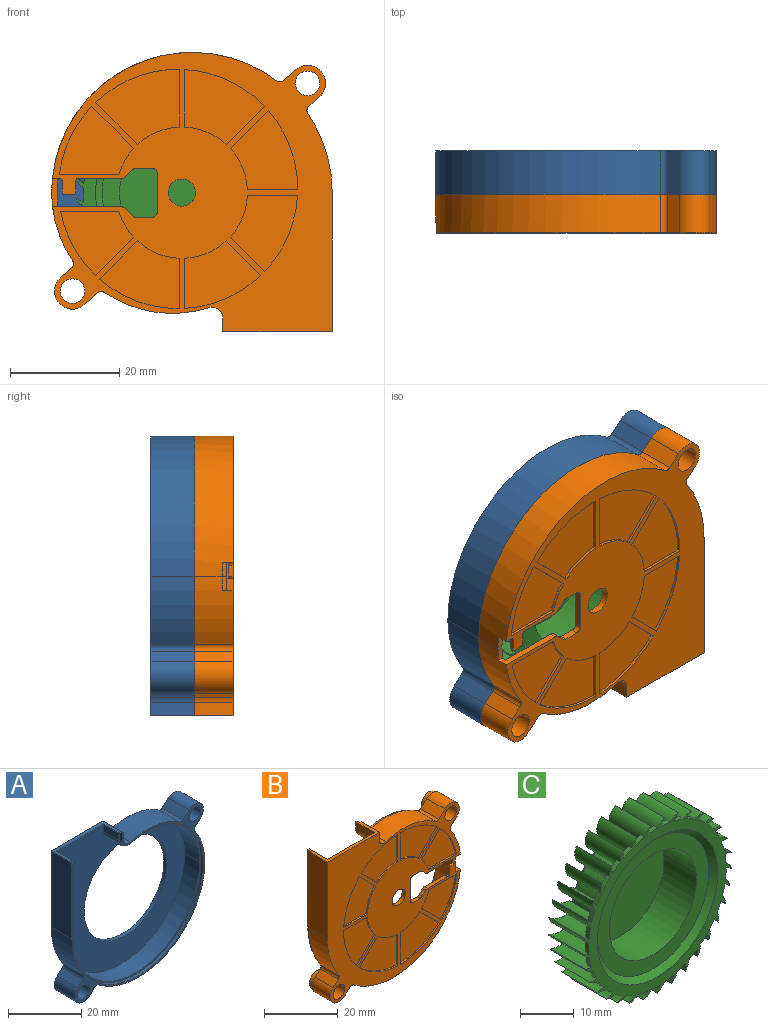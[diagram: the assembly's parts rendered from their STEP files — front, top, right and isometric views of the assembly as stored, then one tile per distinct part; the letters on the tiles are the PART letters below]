
ASSEMBLY  parts=3 mates=2
PART A: 35 faces, bbox 51.3x8x51.1 mm
  f0: cylinder r=25.15mm len=50.3mm, axis (0,-1,0), area 79mm2, adj f28,f32,f33,f34
  f1: cylinder r=2.5mm len=3.25mm, axis (0,-1,0), area 4.7mm2, adj f28,f31,f32,f34
  f2: cylinder r=2.25mm len=8mm, axis (0,1,0), area 113.1mm2, adj f28,f29
  f3: cylinder r=2.25mm len=8mm, axis (0,1,0), area 113.1mm2, adj f28,f29
  f4: cylinder r=22.07mm len=19.05mm, axis (0,1,0), area 159.4mm2, adj f20,f21,f28,f29
  f5: cylinder r=3.3mm len=8mm, axis (0,1,0), area 82.9mm2, adj f18,f19,f28,f29
  f6: cylinder r=1mm len=8mm, axis (0,1,0), area 11mm2, adj f14,f15,f28,f29
  f7: cylinder r=16mm len=32mm, axis (0,1,0), area 120.6mm2, adj f29,f30
  f8: cylinder r=24.65mm len=49.3mm, axis (0,-1,0), area 449.3mm2, adj f11,f12,f30,f34
  f9: cylinder r=3mm len=5.8mm, axis (0,-1,0), area 32.6mm2, adj f10,f11,f30,f34
  f10: plane 5.8x2.44mm, normal (-1,0,0), area 14.2mm2, adj f9,f23,f30,f34
  f11: cylinder r=21.07mm len=27.4mm, axis (0,-1,0), area 229.2mm2, adj f8,f9,f30,f34
  f12: plane 25.4x5.8mm, normal (1,0,0), area 147.3mm2, adj f8,f23,f30,f34
  f13: cylinder r=3.3mm len=8mm, axis (0,1,0), area 82.9mm2, adj f14,f27,f28,f29
  f14: plane 8x2.22mm, normal (0.66,0,-0.75), area 23.7mm2, adj f6,f13,f28,f29
  f15: cylinder r=25.65mm len=41.13mm, axis (0,1,0), area 455.4mm2, adj f6,f16,f28,f29
  f16: cylinder r=22.07mm len=12.41mm, axis (0,1,0), area 105.5mm2, adj f15,f17,f28,f29
  f17: cylinder r=1mm len=8mm, axis (0,1,0), area 11.6mm2, adj f16,f18,f28,f29
  f18: plane 8x2.04mm, normal (0.66,0,-0.75), area 21.8mm2, adj f5,f17,f28,f29
  f19: plane 8x2.44mm, normal (-0.66,0,0.75), area 26mm2, adj f5,f20,f28,f29
  f20: cylinder r=1mm len=8mm, axis (0,1,0), area 10.6mm2, adj f4,f19,f28,f29
  f21: cylinder r=2mm len=8mm, axis (0,1,0), area 30mm2, adj f4,f22,f28,f29
  f22: plane 8x2.44mm, normal (1,0,0), area 19.6mm2, adj f21,f23,f28,f29
  f23: plane 20x8mm, normal (0,0,1), area 36.6mm2, adj f10,f12,f22,f24,f28,f29,f30,f31
  f24: plane 25.4x8mm, normal (-1,0,0), area 203.2mm2, adj f23,f25,f28,f29
  f25: cylinder r=25.65mm len=14.47mm, axis (0,1,0), area 122.9mm2, adj f24,f26,f28,f29
  f26: cylinder r=1mm len=8mm, axis (0,1,0), area 11.6mm2, adj f25,f27,f28,f29
  f27: plane 8x1.98mm, normal (-0.66,0,0.75), area 21.1mm2, adj f13,f26,f28,f29
  f28: plane 51.3x51.07mm, normal (0,-1,0), area 126.8mm2, adj f0,f1,f2,f3,f4,f5,f6,f13
  f29: plane 51.3x51.07mm, normal (0,1,0), area 1370.5mm2, adj f2,f3,f4,f5,f6,f7,f13,f14
  f30: plane 50.07x49.3mm, normal (0,-1,0), area 1168mm2, adj f7,f8,f9,f10,f11,f12,f23
  f31: plane 2.44x1mm, normal (-1,0,0), area 2.4mm2, adj f1,f23,f28,f34
  f32: cylinder r=21.57mm len=28.05mm, axis (0,-1,0), area 40.5mm2, adj f0,f1,f28,f34
  f33: plane 25.4x1mm, normal (1,0,0), area 25.4mm2, adj f0,f23,f28,f34
  f34: plane 50.57x50.3mm, normal (0,-1,0), area 75.6mm2, adj f0,f1,f8,f9,f10,f11,f12,f23
PART B: 104 faces, bbox 52.9x8.5x51.4 mm
  f0: torus R=1.41mm, axis (0,-1,0), area 1.6mm2, adj f31,f35,f102,f103
  f1: cylinder r=21.88mm len=15.3mm, axis (0,-1,0), area 8.4mm2, adj f14,f53,f54,f55
  f2: cylinder r=2.82mm len=5.65mm, axis (0,-1,0), area 26.6mm2, adj f15,f41
  f3: cylinder r=2.82mm len=5.65mm, axis (0,-1,0), area 26.6mm2, adj f15,f40
  f4: cylinder r=21.57mm len=28.05mm, axis (0,1,0), area 40.5mm2, adj f15,f16,f37,f38
  f5: cylinder r=21.07mm len=27.4mm, axis (0,1,0), area 266.7mm2, adj f16,f31,f33,f34,f86,f87
  f6: cylinder r=2.5mm len=5mm, axis (0,-1,0), area 18.8mm2, adj f14,f31
  f7: cylinder r=2.25mm len=8.5mm, axis (0,-1,0), area 120.2mm2, adj f14,f40
  f8: cylinder r=2.25mm len=8.5mm, axis (0,-1,0), area 120.2mm2, adj f14,f41
  f9: cylinder r=25.65mm len=41.13mm, axis (0,-1,0), area 393.3mm2, adj f13,f14,f15,f28,f29,f87
  f10: cylinder r=1mm len=7mm, axis (0,-1,0), area 9.3mm2, adj f14,f15,f23,f24
  f11: cylinder r=2mm len=7mm, axis (0,-1,0), area 26.3mm2, adj f14,f15,f22,f23
  f12: cylinder r=3.3mm len=7mm, axis (0,-1,0), area 72.6mm2, adj f14,f15,f17,f30
  f13: plane 12.66x2mm, normal (0,0,1), area 13.2mm2, adj f9,f14,f31,f34,f87,f93,f95,f98
  f14: plane 51.17x51.07mm, normal (0,-1,0), area 1131.7mm2, adj f1,f6,f7,f8,f9,f10,f11,f12
  f15: plane 51.3x51.07mm, normal (0,1,0), area 108.5mm2, adj f2,f3,f4,f9,f10,f11,f12,f17
  f16: plane 50.57x50.3mm, normal (0,1,0), area 75.6mm2, adj f4,f5,f21,f32,f33,f34,f35,f36
  f17: plane 7x1.98mm, normal (-0.66,0,0.75), area 18.5mm2, adj f12,f14,f15,f18
  f18: cylinder r=1mm len=7mm, axis (0,-1,0), area 10.1mm2, adj f14,f15,f17,f19
  f19: cylinder r=25.65mm len=14.47mm, axis (0,-1,0), area 107.6mm2, adj f14,f15,f18,f20
  f20: plane 25.4x7mm, normal (-1,0,0), area 177.8mm2, adj f14,f15,f19,f21
  f21: plane 20x8mm, normal (0,0,1), area 31.2mm2, adj f14,f15,f16,f20,f22,f32,f35,f36
  f22: plane 7x2.44mm, normal (1,0,0), area 17.1mm2, adj f11,f14,f15,f21
  f23: cylinder r=22.07mm len=19.05mm, axis (0,-1,0), area 139.5mm2, adj f10,f11,f14,f15
  f24: plane 7x2.44mm, normal (-0.66,0,0.75), area 22.8mm2, adj f10,f14,f15,f25
  f25: cylinder r=3.3mm len=7mm, axis (0,-1,0), area 72.6mm2, adj f14,f15,f24,f26
  f26: plane 7x2.04mm, normal (0.66,0,-0.75), area 19.1mm2, adj f14,f15,f25,f27
  f27: cylinder r=1mm len=7mm, axis (0,-1,0), area 10.1mm2, adj f14,f15,f26,f28
  f28: cylinder r=22.07mm len=12.41mm, axis (0,-1,0), area 87.1mm2, adj f9,f14,f15,f27,f86,f87
  f29: cylinder r=1mm len=7mm, axis (0,-1,0), area 9.6mm2, adj f9,f14,f15,f30
  f30: plane 7x2.22mm, normal (0.66,0,-0.75), area 20.7mm2, adj f12,f14,f15,f29
  f31: plane 49.16x46.35mm, normal (0,1,0), area 1650.7mm2, adj f0,f5,f6,f13,f33,f34,f35,f81
  f32: plane 7.1x2.44mm, normal (-1,0,0), area 17.4mm2, adj f16,f21,f33,f102
  f33: cylinder r=3mm len=7.1mm, axis (0,1,0), area 38.5mm2, adj f5,f16,f31,f32,f103
  f34: cylinder r=24.65mm len=49.3mm, axis (0,1,0), area 524.7mm2, adj f5,f13,f16,f31,f35,f87
  f35: plane 25.4x7.1mm, normal (1,0,0), area 179.6mm2, adj f0,f16,f21,f31,f34,f102
  f36: plane 25.4x1mm, normal (-1,0,0), area 25.4mm2, adj f15,f16,f21,f37
  f37: cylinder r=25.15mm len=50.3mm, axis (0,1,0), area 79mm2, adj f4,f15,f16,f36
  f38: cylinder r=2.5mm len=3.25mm, axis (0,1,0), area 4.7mm2, adj f4,f15,f16,f39
  f39: plane 2.44x1mm, normal (1,0,0), area 2.4mm2, adj f15,f16,f21,f38
  f40: plane 5.65x5.65mm, normal (0,1,0), area 9.2mm2, adj f3,f7
  f41: plane 5.65x5.65mm, normal (0,1,0), area 9.2mm2, adj f2,f8
  f42: plane 6.99x6.99mm, normal (0.71,0,-0.71), area 4.9mm2, adj f14,f43,f45,f46
  f43: cylinder r=12mm len=7.62mm, axis (0,-1,0), area 4.2mm2, adj f14,f42,f44,f46
  f44: plane 10.54x0.5mm, normal (-1,0,0), area 5.3mm2, adj f14,f43,f45,f46
  f45: cylinder r=21.88mm len=14.61mm, axis (0,-1,0), area 8.2mm2, adj f14,f42,f44,f46
  f46: plane 14.61x13.7mm, normal (0,-1,0), area 127.2mm2, adj f42,f43,f44,f45
  f47: plane 7.67x7.67mm, normal (0.71,0,0.71), area 5.4mm2, adj f14,f48,f50,f51
  f48: cylinder r=12mm len=4.77mm, axis (0,-1,0), area 2.8mm2, adj f14,f47,f49,f51
  f49: plane 10.88x0.5mm, normal (0,0,-1), area 5.4mm2, adj f14,f48,f50,f51
  f50: cylinder r=21.88mm len=12.45mm, axis (0,-1,0), area 7mm2, adj f14,f47,f49,f51
  f51: plane 13.57x12.45mm, normal (0,-1,0), area 105.4mm2, adj f47,f48,f49,f50
  f52: cylinder r=12mm len=7.62mm, axis (0,-1,0), area 4.2mm2, adj f14,f53,f54,f55
  f53: plane 7.67x7.67mm, normal (-0.71,0,-0.71), area 5.4mm2, adj f1,f14,f52,f55
  f54: plane 10.57x0.5mm, normal (1,0,0), area 5.3mm2, adj f1,f14,f52,f55
  f55: plane 15.3x13.73mm, normal (0,-1,0), area 135.9mm2, adj f1,f52,f53,f54
  f56: cylinder r=12mm len=7.62mm, axis (0,-1,0), area 4.2mm2, adj f14,f57,f59,f60
  f57: plane 9.2x0.5mm, normal (1,0,0), area 4.6mm2, adj f14,f56,f58,f60
  f58: cylinder r=21.88mm len=14.58mm, axis (0,-1,0), area 7.9mm2, adj f14,f57,f59,f60
  f59: plane 6.96x6.96mm, normal (-0.71,0,0.71), area 4.9mm2, adj f14,f56,f58,f60
  f60: plane 14.58x12.36mm, normal (0,-1,0), area 115.4mm2, adj f56,f57,f58,f59
  f61: cylinder r=12mm len=4.77mm, axis (0,-1,0), area 2.8mm2, adj f14,f62,f64,f65
  f62: plane 6.99x6.99mm, normal (0.71,0,-0.71), area 4.9mm2, adj f14,f61,f63,f65
  f63: cylinder r=21.88mm len=11.76mm, axis (0,-1,0), area 6.8mm2, adj f14,f62,f64,f65
  f64: plane 10.66x0.5mm, normal (0,0,1), area 5.3mm2, adj f14,f61,f63,f65
  f65: plane 13.36x11.76mm, normal (0,-1,0), area 97mm2, adj f61,f62,f63,f64
  f66: cylinder r=12mm len=7.62mm, axis (0,-1,0), area 4.2mm2, adj f14,f67,f69,f70
  f67: plane 9.17x0.5mm, normal (0,0,1), area 4.6mm2, adj f14,f66,f68,f70
  f68: cylinder r=21.88mm len=13.93mm, axis (0,-1,0), area 7.7mm2, adj f14,f67,f69,f70
  f69: plane 6.3x6.3mm, normal (-0.71,0,-0.71), area 4.5mm2, adj f14,f66,f68,f70
  f70: plane 13.93x12.33mm, normal (0,-1,0), area 107.6mm2, adj f66,f67,f68,f69
  f71: plane 9.17x0.5mm, normal (-1,0,0), area 4.6mm2, adj f14,f72,f74,f75
  f72: cylinder r=12mm len=7.62mm, axis (0,-1,0), area 4.2mm2, adj f14,f71,f73,f75
  f73: plane 6.3x6.3mm, normal (0.71,0,0.71), area 4.5mm2, adj f14,f72,f74,f75
  f74: cylinder r=21.88mm len=13.93mm, axis (0,-1,0), area 7.7mm2, adj f14,f71,f73,f75
  f75: plane 13.93x12.33mm, normal (0,-1,0), area 107.6mm2, adj f71,f72,f73,f74
  f76: cylinder r=12mm len=7.62mm, axis (0,-1,0), area 4.2mm2, adj f14,f77,f79,f80
  f77: plane 6.96x6.96mm, normal (-0.71,0,0.71), area 4.9mm2, adj f14,f76,f78,f80
  f78: cylinder r=21.88mm len=14.58mm, axis (0,-1,0), area 7.9mm2, adj f14,f77,f79,f80
  f79: plane 9.2x0.5mm, normal (0,0,-1), area 4.6mm2, adj f14,f76,f78,f80
  f80: plane 14.58x12.36mm, normal (0,-1,0), area 115.4mm2, adj f76,f77,f78,f79
  f81: plane 1.31x1.31mm, normal (-0.71,0,0.71), area 2.2mm2, adj f14,f31,f92,f93
  f82: plane 2.79x1.2mm, normal (0,0,1), area 3.3mm2, adj f14,f31,f91,f92
  f83: plane 7x1.2mm, normal (1,0,0), area 8.4mm2, adj f14,f31,f88,f91
  f84: plane 2.79x1.2mm, normal (0,0,-1), area 3.3mm2, adj f14,f31,f88,f90
  f85: plane 1.31x1.31mm, normal (-0.71,0,-0.71), area 2.2mm2, adj f14,f31,f89,f90
  f86: plane 12.63x2mm, normal (0,0,-1), area 16mm2, adj f5,f14,f28,f31,f87,f89
  f87: plane 5.2x1.16mm, normal (0,-1,0), area 5.2mm2, adj f5,f9,f13,f28,f34,f86
  f88: cylinder r=1mm len=1.2mm, axis (0,1,0), area 1.9mm2, adj f14,f31,f83,f84
  f89: cylinder r=1mm len=1.2mm, axis (0,-1,0), area 0.9mm2, adj f14,f31,f85,f86
  f90: cylinder r=1mm len=1.2mm, axis (0,1,0), area 0.9mm2, adj f14,f31,f84,f85
  f91: cylinder r=1mm len=1.2mm, axis (0,1,0), area 1.9mm2, adj f14,f31,f82,f83
  f92: cylinder r=1mm len=1.2mm, axis (0,1,0), area 0.9mm2, adj f14,f31,f81,f82
  f93: cylinder r=1mm len=1.2mm, axis (0,-1,0), area 0.9mm2, adj f13,f14,f31,f81
  f94: plane 2x0.8mm, normal (1,0,0), area 1.6mm2, adj f14,f95,f100,f101
  f95: plane 3.5x3mm, normal (0,1,0), area 7.5mm2, adj f13,f94,f96,f97,f98,f99,f100,f101
  f96: plane 2x0.8mm, normal (-1,0,0), area 1.6mm2, adj f14,f95,f98,f99
  f97: plane 1.5x0.8mm, normal (0,0,1), area 1.2mm2, adj f14,f95,f99,f100
  f98: cylinder r=0.5mm len=0.8mm, axis (0,1,0), area 0.6mm2, adj f13,f14,f95,f96
  f99: cylinder r=0.5mm len=0.8mm, axis (0,1,0), area 0.6mm2, adj f14,f95,f96,f97
  f100: cylinder r=0.5mm len=0.8mm, axis (0,-1,0), area 0.6mm2, adj f14,f94,f95,f97
  f101: cylinder r=0.5mm len=0.8mm, axis (0,-1,0), area 0.6mm2, adj f13,f14,f94,f95
  f102: plane 22.44x18mm, normal (0,1,0), area 150.3mm2, adj f0,f21,f32,f35,f103
  f103: torus R=22.35mm, axis (0,1,0), area 37.3mm2, adj f0,f31,f33,f102
PART C: 207 faces, bbox 39x10.5x38.9 mm
  f0: cylinder r=11.4mm len=22.8mm, axis (0,-1,0), area 608.8mm2, adj f205,f206
  f1: cone r=14.6mm half-angle=45deg, axis (0,-1,0), area 162.1mm2, adj f119,f205
  f2: cylinder r=2.92mm len=9.2mm, axis (0,-1,0), area 52mm2, adj f85,f86,f87,f119,f143,f144
  f3: cylinder r=2.92mm len=9.2mm, axis (0,-1,0), area 52mm2, adj f88,f89,f90,f119,f141,f142
  f4: cylinder r=2.92mm len=9.2mm, axis (0,-1,0), area 52mm2, adj f91,f92,f93,f119,f139,f140
  f5: cylinder r=5.73mm len=9.2mm, axis (0,-1,0), area 44mm2, adj f6,f91,f92,f93,f119,f138
  f6: cylinder r=2.92mm len=9.2mm, axis (0,-1,0), area 52mm2, adj f5,f94,f95,f96,f119,f138
  f7: cylinder r=5.73mm len=9.2mm, axis (0,-1,0), area 44mm2, adj f8,f94,f95,f96,f119,f137
  f8: cylinder r=2.92mm len=9.2mm, axis (0,-1,0), area 52mm2, adj f7,f97,f98,f99,f119,f137
  f9: cylinder r=5.73mm len=9.2mm, axis (0,-1,0), area 44mm2, adj f10,f97,f98,f99,f119,f136
  f10: cylinder r=2.92mm len=9.2mm, axis (0,-1,0), area 52mm2, adj f9,f100,f101,f102,f119,f136
  f11: cylinder r=5.73mm len=9.2mm, axis (0,-1,0), area 44mm2, adj f12,f100,f101,f102,f119,f135
  f12: cylinder r=2.92mm len=9.2mm, axis (0,-1,0), area 52mm2, adj f11,f103,f104,f105,f119,f135
  f13: cylinder r=5.73mm len=9.2mm, axis (0,-1,0), area 44mm2, adj f14,f103,f104,f105,f119,f134
  f14: cylinder r=2.92mm len=9.2mm, axis (0,-1,0), area 52mm2, adj f13,f106,f107,f108,f119,f134
  f15: cylinder r=2.92mm len=9.2mm, axis (0,-1,0), area 52mm2, adj f109,f110,f111,f119,f132,f133
  f16: cylinder r=2.92mm len=9.2mm, axis (0,-1,0), area 52mm2, adj f112,f113,f114,f119,f130,f131
  f17: cylinder r=2.92mm len=9.2mm, axis (0,-1,0), area 52mm2, adj f115,f116,f117,f119,f128,f129
  f18: torus R=11.75mm, axis (0,1,0), area 59.6mm2, adj f19,f121
  f19: cylinder r=12.25mm len=24.5mm, axis (0,-1,0), area 577.3mm2, adj f18,f120
  f20: cone r=14.5mm half-angle=45deg, axis (0,-1,0), area 5.5mm2, adj f118,f120,f123,f125
  f21: cylinder r=18mm len=2.51mm, axis (0,-1,0), area 2.5mm2, adj f118,f119,f123,f125
  f22: cylinder r=18mm len=2.35mm, axis (0,-1,0), area 2.5mm2, adj f24,f119,f200,f202
  f23: cylinder r=18mm len=2.47mm, axis (0,-1,0), area 2.5mm2, adj f25,f119,f122,f203
  f24: plane 2.87x2.61mm, normal (0,1,0), area 4.7mm2, adj f22,f26,f200,f202
  f25: plane 2.53x2.46mm, normal (0,1,0), area 4.7mm2, adj f23,f27,f122,f203
  f26: cone r=14.5mm half-angle=45deg, axis (0,-1,0), area 5.5mm2, adj f24,f120,f200,f202
  f27: cone r=14.5mm half-angle=45deg, axis (0,-1,0), area 5.5mm2, adj f25,f120,f122,f203
  f28: cylinder r=18mm len=2.14mm, axis (0,-1,0), area 2.5mm2, adj f29,f119,f197,f199
  f29: plane 3.17x2.78mm, normal (0,1,0), area 4.7mm2, adj f28,f30,f197,f199
  f30: cone r=14.5mm half-angle=45deg, axis (0,-1,0), area 5.5mm2, adj f29,f120,f197,f199
  f31: cylinder r=18mm len=1.86mm, axis (0,-1,0), area 2.5mm2, adj f32,f119,f194,f196
  f32: plane 3.37x2.85mm, normal (0,1,0), area 4.7mm2, adj f31,f33,f194,f196
  f33: cone r=14.5mm half-angle=45deg, axis (0,-1,0), area 5.5mm2, adj f32,f120,f194,f196
  f34: cylinder r=18mm len=2.01mm, axis (0,-1,0), area 2.5mm2, adj f35,f119,f191,f193
  f35: plane 3.44x2.81mm, normal (0,1,0), area 4.7mm2, adj f34,f36,f191,f193
  f36: cone r=14.5mm half-angle=45deg, axis (0,-1,0), area 5.5mm2, adj f35,f120,f191,f193
  f37: cylinder r=18mm len=2.25mm, axis (0,-1,0), area 2.5mm2, adj f38,f119,f188,f190
  f38: plane 3.38x2.68mm, normal (0,1,0), area 4.7mm2, adj f37,f39,f188,f190
  f39: cone r=14.5mm half-angle=45deg, axis (0,-1,0), area 5.5mm2, adj f38,f120,f188,f190
  f40: cylinder r=18mm len=2.42mm, axis (0,-1,0), area 2.5mm2, adj f41,f119,f185,f187
  f41: plane 3.21x2.44mm, normal (0,1,0), area 4.7mm2, adj f40,f42,f185,f187
  f42: cone r=14.5mm half-angle=45deg, axis (0,-1,0), area 5.5mm2, adj f41,f120,f185,f187
  f43: cylinder r=18mm len=2.5mm, axis (0,-1,0), area 2.5mm2, adj f44,f119,f182,f184
  f44: plane 2.92x2.12mm, normal (0,1,0), area 4.7mm2, adj f43,f45,f182,f184
  f45: cone r=14.5mm half-angle=45deg, axis (0,-1,0), area 5.5mm2, adj f44,f120,f182,f184
  f46: cylinder r=18mm len=2.49mm, axis (0,-1,0), area 2.5mm2, adj f47,f119,f179,f181
  f47: plane 2.6x2.34mm, normal (0,1,0), area 4.7mm2, adj f46,f48,f179,f181
  f48: cone r=14.5mm half-angle=45deg, axis (0,-1,0), area 5.5mm2, adj f47,f120,f179,f181
  f49: cylinder r=18mm len=2.39mm, axis (0,-1,0), area 2.5mm2, adj f50,f119,f176,f178
  f50: plane 2.77x2.56mm, normal (0,1,0), area 4.7mm2, adj f49,f51,f176,f178
  f51: cone r=14.5mm half-angle=45deg, axis (0,-1,0), area 5.5mm2, adj f50,f120,f176,f178
  f52: cylinder r=18mm len=2.2mm, axis (0,-1,0), area 2.5mm2, adj f53,f119,f173,f175
  f53: plane 3.11x2.75mm, normal (0,1,0), area 4.7mm2, adj f52,f54,f173,f175
  f54: cone r=14.5mm half-angle=45deg, axis (0,-1,0), area 5.5mm2, adj f53,f120,f173,f175
  f55: cylinder r=18mm len=1.94mm, axis (0,-1,0), area 2.5mm2, adj f56,f119,f170,f172
  f56: plane 3.33x2.84mm, normal (0,1,0), area 4.7mm2, adj f55,f57,f170,f172
  f57: cone r=14.5mm half-angle=45deg, axis (0,-1,0), area 5.5mm2, adj f56,f120,f170,f172
  f58: cylinder r=18mm len=1.93mm, axis (0,-1,0), area 2.5mm2, adj f59,f119,f167,f169
  f59: plane 3.43x2.83mm, normal (0,1,0), area 4.7mm2, adj f58,f60,f167,f169
  f60: cone r=14.5mm half-angle=45deg, axis (0,-1,0), area 5.5mm2, adj f59,f120,f167,f169
  f61: cylinder r=18mm len=2.2mm, axis (0,-1,0), area 2.5mm2, adj f62,f119,f164,f166
  f62: plane 3.41x2.72mm, normal (0,1,0), area 4.7mm2, adj f61,f63,f164,f166
  f63: cone r=14.5mm half-angle=45deg, axis (0,-1,0), area 5.5mm2, adj f62,f120,f164,f166
  f64: cylinder r=18mm len=2.39mm, axis (0,-1,0), area 2.5mm2, adj f65,f119,f161,f163
  f65: plane 3.26x2.51mm, normal (0,1,0), area 4.7mm2, adj f64,f66,f161,f163
  f66: cone r=14.5mm half-angle=45deg, axis (0,-1,0), area 5.5mm2, adj f65,f120,f161,f163
  f67: cylinder r=18mm len=2.49mm, axis (0,-1,0), area 2.5mm2, adj f68,f119,f158,f160
  f68: plane 3x2.21mm, normal (0,1,0), area 4.7mm2, adj f67,f69,f158,f160
  f69: cone r=14.5mm half-angle=45deg, axis (0,-1,0), area 5.5mm2, adj f68,f120,f158,f160
  f70: cylinder r=18mm len=2.5mm, axis (0,-1,0), area 2.5mm2, adj f71,f119,f155,f157
  f71: plane 2.67x2.22mm, normal (0,1,0), area 4.7mm2, adj f70,f72,f155,f157
  f72: cone r=14.5mm half-angle=45deg, axis (0,-1,0), area 5.5mm2, adj f71,f120,f155,f157
  f73: cylinder r=18mm len=2.42mm, axis (0,-1,0), area 2.5mm2, adj f74,f119,f152,f154
  f74: plane 2.67x2.5mm, normal (0,1,0), area 4.7mm2, adj f73,f75,f152,f154
  f75: cone r=14.5mm half-angle=45deg, axis (0,-1,0), area 5.5mm2, adj f74,f120,f152,f154
  f76: cylinder r=18mm len=2.26mm, axis (0,-1,0), area 2.5mm2, adj f77,f119,f149,f151
  f77: plane 3.04x2.71mm, normal (0,1,0), area 4.7mm2, adj f76,f78,f149,f151
  f78: cone r=14.5mm half-angle=45deg, axis (0,-1,0), area 5.5mm2, adj f77,f120,f149,f151
  f79: cylinder r=18mm len=2.01mm, axis (0,-1,0), area 2.5mm2, adj f80,f119,f146,f148
  f80: plane 3.29x2.83mm, normal (0,1,0), area 4.7mm2, adj f79,f81,f146,f148
  f81: cone r=14.5mm half-angle=45deg, axis (0,-1,0), area 5.5mm2, adj f80,f120,f146,f148
  f82: cylinder r=18mm len=1.85mm, axis (0,-1,0), area 2.5mm2, adj f83,f119,f143,f145
  f83: plane 3.42x2.84mm, normal (0,1,0), area 4.7mm2, adj f82,f84,f143,f145
  f84: cone r=14.5mm half-angle=45deg, axis (0,-1,0), area 5.5mm2, adj f83,f120,f143,f145
  f85: cylinder r=18mm len=2.14mm, axis (0,-1,0), area 2.5mm2, adj f2,f86,f119,f141
  f86: plane 3.43x2.76mm, normal (0,1,0), area 4.7mm2, adj f2,f85,f87,f141
  f87: cone r=14.5mm half-angle=45deg, axis (0,-1,0), area 5.3mm2, adj f2,f86,f120,f141
  f88: cylinder r=18mm len=2.35mm, axis (0,-1,0), area 2.5mm2, adj f3,f89,f119,f139
  f89: plane 3.31x2.57mm, normal (0,1,0), area 4.7mm2, adj f3,f88,f90,f139
  f90: cone r=14.5mm half-angle=45deg, axis (0,-1,0), area 5.3mm2, adj f3,f89,f120,f139
  f91: cylinder r=18mm len=2.47mm, axis (0,-1,0), area 2.5mm2, adj f4,f5,f92,f119
  f92: plane 3.08x2.29mm, normal (0,1,0), area 4.7mm2, adj f4,f5,f91,f93
  f93: cone r=14.5mm half-angle=45deg, axis (0,-1,0), area 5.2mm2, adj f4,f5,f92,f120
  f94: cylinder r=18mm len=2.51mm, axis (0,-1,0), area 2.5mm2, adj f6,f7,f95,f119
  f95: plane 2.74x2.11mm, normal (0,1,0), area 4.7mm2, adj f6,f7,f94,f96
  f96: cone r=14.5mm half-angle=45deg, axis (0,-1,0), area 5.5mm2, adj f6,f7,f95,f120
  f97: cylinder r=18mm len=2.45mm, axis (0,-1,0), area 2.5mm2, adj f8,f9,f98,f119
  f98: plane 2.57x2.48mm, normal (0,1,0), area 4.7mm2, adj f8,f9,f97,f99
  f99: cone r=14.5mm half-angle=45deg, axis (0,-1,0), area 5.5mm2, adj f8,f9,f98,f120
  f100: cylinder r=18mm len=2.31mm, axis (0,-1,0), area 2.5mm2, adj f10,f11,f101,f119
  f101: plane 2.96x2.66mm, normal (0,1,0), area 4.7mm2, adj f10,f11,f100,f102
  f102: cone r=14.5mm half-angle=45deg, axis (0,-1,0), area 5.5mm2, adj f10,f11,f101,f120
  f103: cylinder r=18mm len=2.08mm, axis (0,-1,0), area 2.5mm2, adj f12,f13,f104,f119
  f104: plane 3.23x2.81mm, normal (0,1,0), area 4.7mm2, adj f12,f13,f103,f105
  f105: cone r=14.5mm half-angle=45deg, axis (0,-1,0), area 5.5mm2, adj f12,f13,f104,f120
  f106: cylinder r=18mm len=1.78mm, axis (0,-1,0), area 2.5mm2, adj f14,f107,f119,f132
  f107: plane 3.4x2.85mm, normal (0,1,0), area 4.7mm2, adj f14,f106,f108,f132
  f108: cone r=14.5mm half-angle=45deg, axis (0,-1,0), area 5.5mm2, adj f14,f107,f120,f132
  f109: cylinder r=18mm len=2.08mm, axis (0,-1,0), area 2.5mm2, adj f15,f110,f119,f130
  f110: plane 3.44x2.79mm, normal (0,1,0), area 4.7mm2, adj f15,f109,f111,f130
  f111: cone r=14.5mm half-angle=45deg, axis (0,-1,0), area 5.5mm2, adj f15,f110,f120,f130
  f112: cylinder r=18mm len=2.3mm, axis (0,-1,0), area 2.5mm2, adj f16,f113,f119,f128
  f113: plane 3.35x2.63mm, normal (0,1,0), area 4.7mm2, adj f16,f112,f114,f128
  f114: cone r=14.5mm half-angle=45deg, axis (0,-1,0), area 5.5mm2, adj f16,f113,f120,f128
  f115: cylinder r=18mm len=2.45mm, axis (0,-1,0), area 2.5mm2, adj f17,f116,f119,f126
  f116: plane 3.14x2.37mm, normal (0,1,0), area 4.7mm2, adj f17,f115,f117,f126
  f117: cone r=14.5mm half-angle=45deg, axis (0,-1,0), area 5.5mm2, adj f17,f116,f120,f126
  f118: plane 2.83x2.05mm, normal (0,1,0), area 4.7mm2, adj f20,f21,f123,f125
  f119: plane 38.96x38.91mm, normal (0,-1,0), area 265.7mm2, adj f1,f2,f3,f4,f5,f6,f7,f8
  f120: plane 29x29mm, normal (0,1,0), area 189.1mm2, adj f19,f20,f26,f27,f30,f33,f36,f39
  f121: plane 23.5x23.5mm, normal (0,1,0), area 433.7mm2, adj f18
  f122: cylinder r=2.92mm len=9.2mm, axis (0,-1,0), area 52mm2, adj f23,f25,f27,f119,f123,f124
  f123: cylinder r=5.73mm len=9.2mm, axis (0,-1,0), area 44mm2, adj f20,f21,f118,f119,f122,f124
  f124: plane 5.03x1.97mm, normal (0,1,0), area 3.4mm2, adj f122,f123
  f125: cylinder r=2.92mm len=9.2mm, axis (0,-1,0), area 52mm2, adj f20,f21,f118,f119,f126,f127
  f126: cylinder r=5.73mm len=9.2mm, axis (0,-1,0), area 44mm2, adj f115,f116,f117,f119,f125,f127
  f127: plane 4.77x2.5mm, normal (0,1,0), area 3.4mm2, adj f125,f126
  f128: cylinder r=5.73mm len=9.2mm, axis (0,-1,0), area 44mm2, adj f17,f112,f113,f114,f119,f129
  f129: plane 4.34x3.06mm, normal (0,1,0), area 3.4mm2, adj f17,f128
  f130: cylinder r=5.73mm len=9.2mm, axis (0,-1,0), area 44mm2, adj f16,f109,f110,f111,f119,f131
  f131: plane 3.83x3.61mm, normal (0,1,0), area 3.4mm2, adj f16,f130
  f132: cylinder r=5.73mm len=9.2mm, axis (0,-1,0), area 44mm2, adj f15,f106,f107,f108,f119,f133
  f133: plane 4.13x3.29mm, normal (0,1,0), area 3.4mm2, adj f15,f132
  f134: plane 4.61x2.74mm, normal (0,1,0), area 3.4mm2, adj f13,f14
  f135: plane 4.94x2.19mm, normal (0,1,0), area 3.4mm2, adj f11,f12
  f136: plane 5.09x1.66mm, normal (0,1,0), area 3.4mm2, adj f9,f10
  f137: plane 5.06x1.83mm, normal (0,1,0), area 3.4mm2, adj f7,f8
  f138: plane 4.85x2.37mm, normal (0,1,0), area 3.4mm2, adj f5,f6
  f139: cylinder r=5.73mm len=9.2mm, axis (0,-1,0), area 44mm2, adj f4,f88,f89,f90,f119,f140
  f140: plane 4.46x2.92mm, normal (0,1,0), area 3.4mm2, adj f4,f139
  f141: cylinder r=5.73mm len=9.2mm, axis (0,-1,0), area 44mm2, adj f3,f85,f86,f87,f119,f142
  f142: plane 3.96x3.47mm, normal (0,1,0), area 3.4mm2, adj f3,f141
  f143: cylinder r=5.73mm len=9.2mm, axis (0,-1,0), area 44mm2, adj f2,f82,f83,f84,f119,f144
  f144: plane 4.01x3.43mm, normal (0,1,0), area 3.4mm2, adj f2,f143
  f145: cylinder r=2.92mm len=9.2mm, axis (0,-1,0), area 52mm2, adj f82,f83,f84,f119,f146,f147
  f146: cylinder r=5.73mm len=9.2mm, axis (0,-1,0), area 44mm2, adj f79,f80,f81,f119,f145,f147
  f147: plane 4.5x2.87mm, normal (0,1,0), area 3.4mm2, adj f145,f146
  f148: cylinder r=2.92mm len=9.2mm, axis (0,-1,0), area 52mm2, adj f79,f80,f81,f119,f149,f150
  f149: cylinder r=5.73mm len=9.2mm, axis (0,-1,0), area 44mm2, adj f76,f77,f78,f119,f148,f150
  f150: plane 4.87x2.32mm, normal (0,1,0), area 3.4mm2, adj f148,f149
  f151: cylinder r=2.92mm len=9.2mm, axis (0,-1,0), area 52mm2, adj f76,f77,f78,f119,f152,f153
  f152: cylinder r=5.73mm len=9.2mm, axis (0,-1,0), area 44mm2, adj f73,f74,f75,f119,f151,f153
  f153: plane 5.07x1.79mm, normal (0,1,0), area 3.4mm2, adj f151,f152
  f154: cylinder r=2.92mm len=9.2mm, axis (0,-1,0), area 52mm2, adj f73,f74,f75,f119,f155,f156
  f155: cylinder r=5.73mm len=9.2mm, axis (0,-1,0), area 44mm2, adj f70,f71,f72,f119,f154,f156
  f156: plane 5.09x1.71mm, normal (0,1,0), area 3.4mm2, adj f154,f155
  f157: cylinder r=2.92mm len=9.2mm, axis (0,-1,0), area 52mm2, adj f70,f71,f72,f119,f158,f159
  f158: cylinder r=5.73mm len=9.2mm, axis (0,-1,0), area 44mm2, adj f67,f68,f69,f119,f157,f159
  f159: plane 4.92x2.23mm, normal (0,1,0), area 3.4mm2, adj f157,f158
  f160: cylinder r=2.92mm len=9.2mm, axis (0,-1,0), area 52mm2, adj f67,f68,f69,f119,f161,f162
  f161: cylinder r=5.73mm len=9.2mm, axis (0,-1,0), area 44mm2, adj f64,f65,f66,f119,f160,f162
  f162: plane 4.57x2.78mm, normal (0,1,0), area 3.4mm2, adj f160,f161
  f163: cylinder r=2.92mm len=9.2mm, axis (0,-1,0), area 52mm2, adj f64,f65,f66,f119,f164,f165
  f164: cylinder r=5.73mm len=9.2mm, axis (0,-1,0), area 44mm2, adj f61,f62,f63,f119,f163,f165
  f165: plane 4.09x3.34mm, normal (0,1,0), area 3.4mm2, adj f163,f164
  f166: cylinder r=2.92mm len=9.2mm, axis (0,-1,0), area 52mm2, adj f61,f62,f63,f119,f167,f168
  f167: cylinder r=5.73mm len=9.2mm, axis (0,-1,0), area 44mm2, adj f58,f59,f60,f119,f166,f168
  f168: plane 3.88x3.56mm, normal (0,1,0), area 3.4mm2, adj f166,f167
  f169: cylinder r=2.92mm len=9.2mm, axis (0,-1,0), area 52mm2, adj f58,f59,f60,f119,f170,f171
  f170: cylinder r=5.73mm len=9.2mm, axis (0,-1,0), area 44mm2, adj f55,f56,f57,f119,f169,f171
  f171: plane 4.38x3.01mm, normal (0,1,0), area 3.4mm2, adj f169,f170
  f172: cylinder r=2.92mm len=9.2mm, axis (0,-1,0), area 52mm2, adj f55,f56,f57,f119,f173,f174
  f173: cylinder r=5.73mm len=9.2mm, axis (0,-1,0), area 44mm2, adj f52,f53,f54,f119,f172,f174
  f174: plane 4.8x2.46mm, normal (0,1,0), area 3.4mm2, adj f172,f173
  f175: cylinder r=2.92mm len=9.2mm, axis (0,-1,0), area 52mm2, adj f52,f53,f54,f119,f176,f177
  f176: cylinder r=5.73mm len=9.2mm, axis (0,-1,0), area 44mm2, adj f49,f50,f51,f119,f175,f177
  f177: plane 5.04x1.92mm, normal (0,1,0), area 3.4mm2, adj f175,f176
  f178: cylinder r=2.92mm len=9.2mm, axis (0,-1,0), area 52mm2, adj f49,f50,f51,f119,f179,f180
  f179: cylinder r=5.73mm len=9.2mm, axis (0,-1,0), area 44mm2, adj f46,f47,f48,f119,f178,f180
  f180: plane 5.1x1.58mm, normal (0,1,0), area 3.4mm2, adj f178,f179
  f181: cylinder r=2.92mm len=9.2mm, axis (0,-1,0), area 52mm2, adj f46,f47,f48,f119,f182,f183
  f182: cylinder r=5.73mm len=9.2mm, axis (0,-1,0), area 44mm2, adj f43,f44,f45,f119,f181,f183
  f183: plane 4.98x2.1mm, normal (0,1,0), area 3.4mm2, adj f181,f182
  f184: cylinder r=2.92mm len=9.2mm, axis (0,-1,0), area 52mm2, adj f43,f44,f45,f119,f185,f186
  f185: cylinder r=5.73mm len=9.2mm, axis (0,-1,0), area 44mm2, adj f40,f41,f42,f119,f184,f186
  f186: plane 4.68x2.64mm, normal (0,1,0), area 3.4mm2, adj f184,f185
  f187: cylinder r=2.92mm len=9.2mm, axis (0,-1,0), area 52mm2, adj f40,f41,f42,f119,f188,f189
  f188: cylinder r=5.73mm len=9.2mm, axis (0,-1,0), area 44mm2, adj f37,f38,f39,f119,f187,f189
  f189: plane 4.22x3.2mm, normal (0,1,0), area 3.4mm2, adj f187,f188
  f190: cylinder r=2.92mm len=9.2mm, axis (0,-1,0), area 52mm2, adj f37,f38,f39,f119,f191,f192
  f191: cylinder r=5.73mm len=9.2mm, axis (0,-1,0), area 44mm2, adj f34,f35,f36,f119,f190,f192
  f192: plane 3.74x3.7mm, normal (0,1,0), area 3.4mm2, adj f190,f191
  f193: cylinder r=2.92mm len=9.2mm, axis (0,-1,0), area 52mm2, adj f34,f35,f36,f119,f194,f195
  f194: cylinder r=5.73mm len=9.2mm, axis (0,-1,0), area 44mm2, adj f31,f32,f33,f119,f193,f195
  f195: plane 4.26x3.15mm, normal (0,1,0), area 3.4mm2, adj f193,f194
  f196: cylinder r=2.92mm len=9.2mm, axis (0,-1,0), area 52mm2, adj f31,f32,f33,f119,f197,f198
  f197: cylinder r=5.73mm len=9.2mm, axis (0,-1,0), area 44mm2, adj f28,f29,f30,f119,f196,f198
  f198: plane 4.71x2.6mm, normal (0,1,0), area 3.4mm2, adj f196,f197
  f199: cylinder r=2.92mm len=9.2mm, axis (0,-1,0), area 52mm2, adj f28,f29,f30,f119,f200,f201
  f200: cylinder r=5.73mm len=9.2mm, axis (0,-1,0), area 44mm2, adj f22,f24,f26,f119,f199,f201
  f201: plane 5x2.05mm, normal (0,1,0), area 3.4mm2, adj f199,f200
  f202: cylinder r=2.92mm len=9.2mm, axis (0,-1,0), area 52mm2, adj f22,f24,f26,f119,f203,f204
  f203: cylinder r=5.73mm len=9.2mm, axis (0,-1,0), area 44mm2, adj f23,f25,f27,f119,f202,f204
  f204: plane 5.1x1.54mm, normal (0,1,0), area 3.4mm2, adj f202,f203
  f205: plane 29.2x29.2mm, normal (0,-1,0), area 261.4mm2, adj f0,f1
  f206: plane 22.8x22.8mm, normal (0,-1,0), area 408.3mm2, adj f0
PLACE A rot(axis=(0,1,0),180deg) t=(19.7,12.38,26.77)mm
PLACE B rot(axis=(0,1,0),180deg) t=(19.7,-2.62,26.77)mm fixed
PLACE C rot(axis=(0,-1,0),0deg) t=(19.7,1.38,26.77)mm
MATE fastened C.f0 <-> B.f6  axis (0,-1,0) through (19.7,2.58,26.77)mm
MATE fastened A.f3 <-> B.f2  axis (0,-1,0) through (42.7,4.38,46.77)mm
